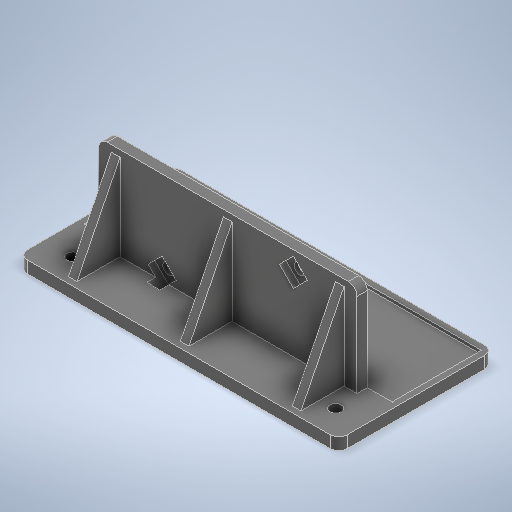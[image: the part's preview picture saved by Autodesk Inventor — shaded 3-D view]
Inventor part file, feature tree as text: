
AUTODESK INVENTOR PART (.ipt)
format: ipt  version: 2025 (Build 290162000, 162)  size: 360,960 bytes
history: native  units: mm
features: sketch x7, extrude x4, hole x2, projected_geometry x2, rib x1, pattern_linear x1, fillet x1
ambient origin geometry x8: Origin, YZ Plane, XZ Plane, XY Plane, X Axis, Y Axis, Z Axis, Center Point
bodies: Solid1 (feature_tree)
feature tree (18):
  extrude  "Extrusion1"  Depth=89.8mm
  extrude  "Extrusion2"  Depth=178.8mm
  extrude  "Extrusion3"  Depth=3.5mm
  hole  "Hole1"  [1 undecoded]
  extrude  "Extrusion4"  Depth=6.0mm
  rib  "Rib1"
  pattern_linear  "Rectangular Pattern1"  Spacing1=76.2mm  [1 undecoded]
  hole  "Hole2"  [1 undecoded]
  fillet  "Fillet1"  Radius=11.43mm
  sketch  "Sketch1"  dims[d0=185.8mm d1=89.8mm]
  sketch  "Sketch2"  dims[d2=7.0mm d3=0.0mm d4=178.8mm]
  sketch  "Sketch3"  dims[d6=51.8mm d7=3.5mm]
  sketch  "Sketch4"  dims[d8=2.0mm d9=0.0mm d10=150.0mm]
  sketch  "Sketch5"  dims[d11=75.0mm d12=6.0mm]
  projected_geometry  "Projected Loop1"
  sketch  "Sketch6"  dims[d13=53.8mm d14=0.0mm]
  projected_geometry  "Projected Loop2"
  sketch  "Sketch7"  dims[d15=36.9mm d17=76.2mm d18=38.1mm d19=6.756mm d20=6.0mm d21=11.113mm d22=6.35mm d23=90.0deg d24=19.05mm d25=20.594885mm d26=11.43mm d27=45.0deg d28=11.43mm d29=11.43mm d30=45.0deg d31=11.43mm d32=6.35mm d33=5.08mm d34=3.81mm d35=0.0mm d36=0.0mm d37=50.0mm d38=25.0mm d39=1.0mm d40=5.0mm d41=0.0mm d42=0.0mm d43=1.0mm d44=1.0mm d45=30.0mm d47=65.0mm d48=76.2mm d49=76.2mm d50=30.0mm d51=6.756mm d52=6.0mm d53=4.0mm d54=2.0mm d55=90.0deg d56=19.05mm d57=20.594885mm d58=5.0mm]
note: 3 required parameter values undecoded (feature->parameter linkage not recoverable at this tier; creation-order binding heuristic only, values carry confidence <= 0.55)
